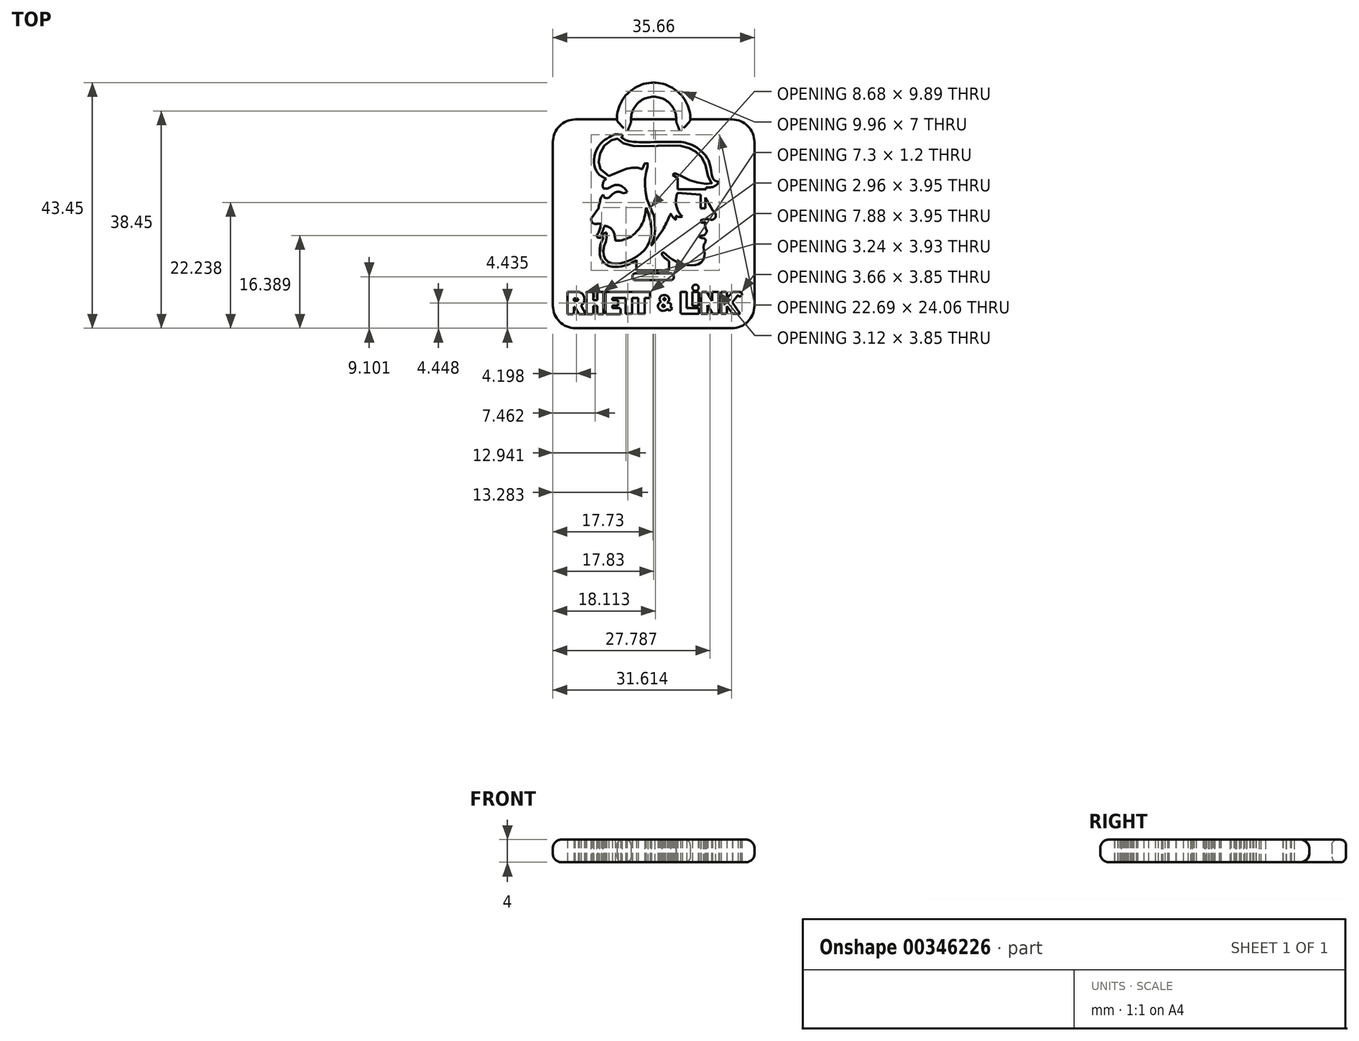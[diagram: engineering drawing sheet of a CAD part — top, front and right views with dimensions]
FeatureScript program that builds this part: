
annotation { "Feature Type Name" : "Feature", "Feature Type Description" : "" }
export const myFeature = defineFeature(function(context is Context, id is Id, definition is map)
    precondition{}
    {
        {
            var Q0;
            Q0=qCreatedBy(makeId("Top.planeOp"),FACE);
            var sketch = newSketch(context, id + "F0", { "sketchPlane" : qUnion([Q0])});
            skFitSpline(sketch, "E0", {"points": [v(13.7, 33.26) * mm, v(12.24, 34.54) * mm, v(11.94, 35.46) * mm, v(12.01, 36.74) * mm, v(12.51, 38.04) * mm, v(13.53, 39.18) * mm, v(14.57, 39.78) * mm, v(15.22, 39.92) * mm, v(15.44, 39.53) * mm, v(17.1, 38.8) * mm, v(18.7, 38.6) * mm, v(21.72, 38.6) * mm, v(24.02, 38.67) * mm, v(26.42, 38.61) * mm, v(27.65, 38.32) * mm, v(28.66, 37.89) * mm, v(29.6, 37.23) * mm, v(30.3, 36.36) * mm, v(30.89, 35.02) * mm, v(31.44, 32.77) * mm, v(31.88, 31.99) * mm, v(31.48, 31.9) * mm, v(30.69, 31.9) * mm, v(29.3, 32.16) * mm, v(28.17, 32.45) * mm, v(27.15, 32.9) * mm, v(25.4, 33.87) * mm, v(25.3, 33.81) * mm], "startDerivative": vector(-77.71, 44.4) * mm, "endDerivative": vector(-18.68, -15.52) * mm});
            skLineSegment(sketch, "E1", {"start": v(25.3, 33.81) * mm, "end": v(25.02, 33.46) * mm});
            skLineSegment(sketch, "E2", {"start": v(25.02, 33.46) * mm, "end": v(25.9, 32.88) * mm});
            skLineSegment(sketch, "E3", {"start": v(25.9, 32.88) * mm, "end": v(25.9, 30.92) * mm});
            skLineSegment(sketch, "E4", {"start": v(25.9, 30.92) * mm, "end": v(30.9, 30.92) * mm});
            skLineSegment(sketch, "E5", {"start": v(30.9, 30.92) * mm, "end": v(30.9, 31.22) * mm});
            skLineSegment(sketch, "E6", {"start": v(30.9, 31.22) * mm, "end": v(31.24, 31.22) * mm});
            skLineSegment(sketch, "E7", {"start": v(25.87, 30.3) * mm, "end": v(29.94, 29.97) * mm});
            skLineSegment(sketch, "E8", {"start": v(29.94, 29.97) * mm, "end": v(29.94, 27.54) * mm});
            skLineSegment(sketch, "E9", {"start": v(29.94, 27.54) * mm, "end": v(30.81, 27.54) * mm});
            skLineSegment(sketch, "E10", {"start": v(30.81, 27.54) * mm, "end": v(30.81, 29.46) * mm});
            skLineSegment(sketch, "E11", {"start": v(30.81, 29.46) * mm, "end": v(31.98, 27.34) * mm});
            skLineSegment(sketch, "E12", {"start": v(18.62, 18.44) * mm, "end": v(18.62, 16.55) * mm});
            skLineSegment(sketch, "E13", {"start": v(18.62, 16.55) * mm, "end": v(24.35, 16.55) * mm});
            skLineSegment(sketch, "E14", {"start": v(24.35, 16.55) * mm, "end": v(24.35, 18.23) * mm});
            skLineSegment(sketch, "E15.bottom", {"start": v(18.4, 16.04) * mm, "end": v(24.7, 16.04) * mm});
            skLineSegment(sketch, "E15.top", {"start": v(18.4, 14.84) * mm, "end": v(24.7, 14.84) * mm});
            skLineSegment(sketch, "E15.left", {"start": v(17.9, 15.54) * mm, "end": v(17.9, 15.34) * mm});
            skLineSegment(sketch, "E15.right", {"start": v(25.2, 15.54) * mm, "end": v(25.2, 15.34) * mm});
            skPoint(sketch, "E16.visualSharp", {"position": v(17.9, 16.04) * mm});
            skArc(sketch, "E16.filletArc", {"start": v(18.4, 16.04) * mm, "mid": v(18.05, 15.9) * mm, "end": v(17.9, 15.54) * mm});
            skPoint(sketch, "E17.visualSharp", {"position": v(17.9, 14.84) * mm});
            skArc(sketch, "E17.filletArc", {"start": v(17.9, 15.34) * mm, "mid": v(18.05, 14.99) * mm, "end": v(18.4, 14.84) * mm});
            skPoint(sketch, "E18.visualSharp", {"position": v(25.2, 16.04) * mm});
            skArc(sketch, "E18.filletArc", {"start": v(25.2, 15.54) * mm, "mid": v(25.05, 15.9) * mm, "end": v(24.7, 16.04) * mm});
            skPoint(sketch, "E19.visualSharp", {"position": v(25.2, 14.84) * mm});
            skArc(sketch, "E19.filletArc", {"start": v(24.7, 14.84) * mm, "mid": v(25.05, 14.99) * mm, "end": v(25.2, 15.34) * mm});
            skLineSegment(sketch, "E20", {"start": v(7.22, 8.81) * mm, "end": v(6.4, 8.81) * mm});
            skLineSegment(sketch, "E21", {"start": v(6.4, 8.81) * mm, "end": v(6.4, 12.74) * mm});
            skLineSegment(sketch, "E22", {"start": v(6.4, 12.74) * mm, "end": v(8.5, 12.74) * mm});
            skLineSegment(sketch, "E23", {"start": v(8.07, 11.6) * mm, "end": v(7.55, 11.6) * mm});
            skLineSegment(sketch, "E24", {"start": v(7.55, 11.6) * mm, "end": v(7.55, 11.18) * mm});
            skLineSegment(sketch, "E25", {"start": v(7.55, 11.18) * mm, "end": v(8.07, 11.18) * mm});
            skLineSegment(sketch, "E26", {"start": v(7.52, 9.11) * mm, "end": v(7.52, 10.11) * mm});
            skLineSegment(sketch, "E27", {"start": v(7.52, 10.11) * mm, "end": v(7.74, 10.11) * mm});
            skLineSegment(sketch, "E28", {"start": v(7.74, 10.11) * mm, "end": v(8.45, 8.81) * mm});
            skLineSegment(sketch, "E29", {"start": v(8.45, 8.81) * mm, "end": v(9.64, 8.81) * mm});
            skLineSegment(sketch, "E30", {"start": v(10.96, 11.31) * mm, "end": v(10.96, 12.46) * mm});
            skLineSegment(sketch, "E31", {"start": v(10.66, 12.76) * mm, "end": v(9.8, 12.76) * mm});
            skLineSegment(sketch, "E32", {"start": v(9.8, 12.76) * mm, "end": v(9.8, 8.81) * mm});
            skLineSegment(sketch, "E33", {"start": v(9.8, 8.81) * mm, "end": v(10.66, 8.81) * mm});
            skLineSegment(sketch, "E34", {"start": v(10.96, 9.11) * mm, "end": v(10.96, 10.29) * mm});
            skLineSegment(sketch, "E35", {"start": v(10.96, 10.29) * mm, "end": v(11.7, 10.29) * mm});
            skLineSegment(sketch, "E36", {"start": v(11.7, 10.29) * mm, "end": v(11.7, 9.11) * mm});
            skLineSegment(sketch, "E37", {"start": v(12, 8.81) * mm, "end": v(12.76, 8.81) * mm});
            skLineSegment(sketch, "E38", {"start": v(12.76, 8.81) * mm, "end": v(12.76, 12.76) * mm});
            skLineSegment(sketch, "E39", {"start": v(12.76, 12.76) * mm, "end": v(12, 12.76) * mm});
            skLineSegment(sketch, "E40", {"start": v(11.7, 12.46) * mm, "end": v(11.7, 11.31) * mm});
            skLineSegment(sketch, "E41", {"start": v(11.7, 11.31) * mm, "end": v(10.96, 11.31) * mm});
            skLineSegment(sketch, "E42", {"start": v(13.16, 12.46) * mm, "end": v(13.16, 9.11) * mm});
            skLineSegment(sketch, "E43", {"start": v(13.46, 8.81) * mm, "end": v(15.8, 8.81) * mm});
            skLineSegment(sketch, "E44", {"start": v(15.8, 8.81) * mm, "end": v(15.8, 9.6) * mm});
            skLineSegment(sketch, "E45", {"start": v(15.5, 9.9) * mm, "end": v(14.31, 9.9) * mm});
            skLineSegment(sketch, "E46", {"start": v(14.31, 9.9) * mm, "end": v(14.31, 10.36) * mm});
            skLineSegment(sketch, "E47", {"start": v(14.31, 10.36) * mm, "end": v(15.38, 10.36) * mm});
            skLineSegment(sketch, "E48", {"start": v(15.38, 10.36) * mm, "end": v(15.38, 11.28) * mm});
            skLineSegment(sketch, "E49", {"start": v(15.38, 11.28) * mm, "end": v(14.31, 11.28) * mm});
            skLineSegment(sketch, "E50", {"start": v(14.31, 11.28) * mm, "end": v(14.31, 11.71) * mm});
            skLineSegment(sketch, "E51", {"start": v(14.31, 11.71) * mm, "end": v(16.7, 11.71) * mm});
            skLineSegment(sketch, "E52", {"start": v(16.7, 11.71) * mm, "end": v(16.7, 8.91) * mm});
            skLineSegment(sketch, "E53", {"start": v(16.7, 8.91) * mm, "end": v(17.85, 8.91) * mm});
            skLineSegment(sketch, "E54", {"start": v(17.85, 8.91) * mm, "end": v(17.85, 11.71) * mm});
            skLineSegment(sketch, "E55", {"start": v(17.85, 11.71) * mm, "end": v(18.92, 11.71) * mm});
            skLineSegment(sketch, "E56", {"start": v(18.92, 11.71) * mm, "end": v(18.92, 8.91) * mm});
            skLineSegment(sketch, "E57", {"start": v(18.92, 8.91) * mm, "end": v(20.05, 8.91) * mm});
            skLineSegment(sketch, "E58", {"start": v(20.05, 8.91) * mm, "end": v(20.05, 11.71) * mm});
            skLineSegment(sketch, "E59", {"start": v(20.05, 11.71) * mm, "end": v(21.04, 11.71) * mm});
            skLineSegment(sketch, "E60", {"start": v(21.04, 11.71) * mm, "end": v(21.04, 12.76) * mm});
            skLineSegment(sketch, "E61", {"start": v(21.04, 12.76) * mm, "end": v(13.46, 12.76) * mm});
            skLineSegment(sketch, "E62", {"start": v(24.07, 9.75) * mm, "end": v(24.43, 9.42) * mm});
            skLineSegment(sketch, "E63", {"start": v(24.43, 9.42) * mm, "end": v(24.95, 9.86) * mm});
            skLineSegment(sketch, "E64", {"start": v(24.95, 9.86) * mm, "end": v(24.58, 10.2) * mm});
            skLineSegment(sketch, "E65", {"start": v(24.58, 10.2) * mm, "end": v(24.85, 10.5) * mm});
            skLineSegment(sketch, "E66", {"start": v(24.85, 10.5) * mm, "end": v(24.44, 10.87) * mm});
            skLineSegment(sketch, "E67", {"start": v(24.44, 10.87) * mm, "end": v(24.22, 10.72) * mm});
            skLineSegment(sketch, "E68", {"start": v(24.22, 10.72) * mm, "end": v(24.06, 10.86) * mm});
            skLineSegment(sketch, "E69", {"start": v(23.67, 10.23) * mm, "end": v(23.35, 10.55) * mm});
            skLineSegment(sketch, "E70", {"start": v(26.4, 12.76) * mm, "end": v(26.4, 9.21) * mm});
            skLineSegment(sketch, "E71", {"start": v(26.7, 8.91) * mm, "end": v(29.66, 8.91) * mm});
            skLineSegment(sketch, "E72", {"start": v(29.66, 8.91) * mm, "end": v(29.66, 9.9) * mm});
            skLineSegment(sketch, "E73", {"start": v(29.66, 9.9) * mm, "end": v(27.5, 9.9) * mm});
            skLineSegment(sketch, "E74", {"start": v(27.5, 9.9) * mm, "end": v(27.5, 12.76) * mm});
            skLineSegment(sketch, "E75", {"start": v(27.5, 12.76) * mm, "end": v(26.4, 12.76) * mm});
            skLineSegment(sketch, "E76", {"start": v(28.51, 12.76) * mm, "end": v(28.51, 10.27) * mm});
            skLineSegment(sketch, "E77", {"start": v(28.51, 10.27) * mm, "end": v(29.61, 10.27) * mm});
            skLineSegment(sketch, "E78", {"start": v(29.61, 10.27) * mm, "end": v(29.61, 12.76) * mm});
            skLineSegment(sketch, "E79", {"start": v(29.61, 12.76) * mm, "end": v(28.51, 12.76) * mm});
            skCircle(sketch, "E80", {"center": v(29.06, 13.5) * mm, "radius": 0.55 * mm});
            skLineSegment(sketch, "E81", {"start": v(30.05, 8.91) * mm, "end": v(30.05, 12.46) * mm});
            skLineSegment(sketch, "E82", {"start": v(30.35, 12.76) * mm, "end": v(31.01, 12.76) * mm});
            skLineSegment(sketch, "E83", {"start": v(31.01, 12.76) * mm, "end": v(32, 11.17) * mm});
            skLineSegment(sketch, "E84", {"start": v(32, 11.17) * mm, "end": v(32, 12.76) * mm});
            skLineSegment(sketch, "E85", {"start": v(32, 12.76) * mm, "end": v(33.17, 12.76) * mm});
            skLineSegment(sketch, "E86", {"start": v(33.17, 12.76) * mm, "end": v(33.17, 9.21) * mm});
            skLineSegment(sketch, "E87", {"start": v(32.87, 8.91) * mm, "end": v(32.08, 8.91) * mm});
            skLineSegment(sketch, "E88", {"start": v(32.08, 8.91) * mm, "end": v(31.15, 10.42) * mm});
            skLineSegment(sketch, "E89", {"start": v(31.15, 10.42) * mm, "end": v(31.15, 8.91) * mm});
            skLineSegment(sketch, "E90", {"start": v(31.15, 8.91) * mm, "end": v(30.05, 8.91) * mm});
            skLineSegment(sketch, "E91", {"start": v(33.6, 12.76) * mm, "end": v(33.6, 8.91) * mm});
            skLineSegment(sketch, "E92", {"start": v(33.6, 8.91) * mm, "end": v(34.32, 8.91) * mm});
            skLineSegment(sketch, "E93", {"start": v(34.62, 9.21) * mm, "end": v(34.62, 10.23) * mm});
            skLineSegment(sketch, "E94", {"start": v(34.62, 10.23) * mm, "end": v(35.62, 8.91) * mm});
            skLineSegment(sketch, "E95", {"start": v(35.62, 8.91) * mm, "end": v(36.94, 8.91) * mm});
            skLineSegment(sketch, "E96", {"start": v(36.94, 8.91) * mm, "end": v(35.54, 10.93) * mm});
            skLineSegment(sketch, "E97", {"start": v(35.54, 10.93) * mm, "end": v(37, 12.76) * mm});
            skLineSegment(sketch, "E98", {"start": v(37, 12.76) * mm, "end": v(35.6, 12.76) * mm});
            skLineSegment(sketch, "E99", {"start": v(35.6, 12.76) * mm, "end": v(34.62, 11.63) * mm});
            skLineSegment(sketch, "E100", {"start": v(34.62, 11.63) * mm, "end": v(34.62, 12.46) * mm});
            skLineSegment(sketch, "E101", {"start": v(34.32, 12.76) * mm, "end": v(33.6, 12.76) * mm});
            skCircle(sketch, "E102", {"center": v(36.9, 12.33) * mm, "radius": 0.37 * mm});
            skArc(sketch, "E103", {"start": v(8.07, 11.6) * mm, "mid": v(8.29, 11.39) * mm, "end": v(8.07, 11.18) * mm});
            skPoint(sketch, "E104.visualSharp", {"position": v(7.52, 8.81) * mm});
            skArc(sketch, "E104.filletArc", {"start": v(7.22, 8.81) * mm, "mid": v(7.44, 8.9) * mm, "end": v(7.52, 9.11) * mm});
            skPoint(sketch, "E105.visualSharp", {"position": v(10.96, 8.81) * mm});
            skArc(sketch, "E105.filletArc", {"start": v(10.66, 8.81) * mm, "mid": v(10.88, 8.9) * mm, "end": v(10.96, 9.11) * mm});
            skPoint(sketch, "E106.visualSharp", {"position": v(11.7, 8.81) * mm});
            skArc(sketch, "E106.filletArc", {"start": v(11.7, 9.11) * mm, "mid": v(11.79, 8.9) * mm, "end": v(12, 8.81) * mm});
            skPoint(sketch, "E107.visualSharp", {"position": v(10.96, 12.76) * mm});
            skArc(sketch, "E107.filletArc", {"start": v(10.96, 12.46) * mm, "mid": v(10.88, 12.68) * mm, "end": v(10.66, 12.76) * mm});
            skPoint(sketch, "E108.visualSharp", {"position": v(11.7, 12.76) * mm});
            skArc(sketch, "E108.filletArc", {"start": v(12, 12.76) * mm, "mid": v(11.79, 12.68) * mm, "end": v(11.7, 12.46) * mm});
            skPoint(sketch, "E109.visualSharp", {"position": v(13.16, 8.81) * mm});
            skArc(sketch, "E109.filletArc", {"start": v(13.16, 9.11) * mm, "mid": v(13.25, 8.9) * mm, "end": v(13.46, 8.81) * mm});
            skPoint(sketch, "E110.visualSharp", {"position": v(13.16, 12.76) * mm});
            skArc(sketch, "E110.filletArc", {"start": v(13.46, 12.76) * mm, "mid": v(13.25, 12.68) * mm, "end": v(13.16, 12.46) * mm});
            skPoint(sketch, "E111.visualSharp", {"position": v(15.8, 9.9) * mm});
            skArc(sketch, "E111.filletArc", {"start": v(15.8, 9.6) * mm, "mid": v(15.71, 9.81) * mm, "end": v(15.5, 9.9) * mm});
            skPoint(sketch, "E112.visualSharp", {"position": v(26.4, 8.91) * mm});
            skArc(sketch, "E112.filletArc", {"start": v(26.4, 9.21) * mm, "mid": v(26.48, 9) * mm, "end": v(26.7, 8.91) * mm});
            skPoint(sketch, "E113.visualSharp", {"position": v(33.17, 8.91) * mm});
            skArc(sketch, "E113.filletArc", {"start": v(32.87, 8.91) * mm, "mid": v(33.08, 9) * mm, "end": v(33.17, 9.21) * mm});
            skPoint(sketch, "E114.visualSharp", {"position": v(30.05, 12.76) * mm});
            skArc(sketch, "E114.filletArc", {"start": v(30.35, 12.76) * mm, "mid": v(30.13, 12.68) * mm, "end": v(30.05, 12.46) * mm});
            skPoint(sketch, "E115.visualSharp", {"position": v(34.62, 8.91) * mm});
            skArc(sketch, "E115.filletArc", {"start": v(34.32, 8.91) * mm, "mid": v(34.53, 9) * mm, "end": v(34.62, 9.21) * mm});
            skPoint(sketch, "E116.visualSharp", {"position": v(34.62, 12.76) * mm});
            skArc(sketch, "E116.filletArc", {"start": v(34.62, 12.46) * mm, "mid": v(34.53, 12.68) * mm, "end": v(34.32, 12.76) * mm});
            skLineSegment(sketch, "E117", {"start": v(9.64, 8.81) * mm, "end": v(8.8, 10.36) * mm});
            skFitSpline(sketch, "E118", {"points": [v(8.5, 12.74) * mm, v(9.01, 12.48) * mm, v(9.36, 11.79) * mm, v(9.33, 11) * mm, v(9.14, 10.66) * mm, v(8.8, 10.36) * mm], "startDerivative": vector(2.6, -0.63) * mm, "endDerivative": vector(-2.15, -1.69) * mm});
            skFitSpline(sketch, "E119", {"points": [v(24.07, 9.75) * mm, v(23.83, 9.54) * mm, v(23.13, 9.45) * mm, v(22.51, 9.85) * mm, v(22.4, 10.32) * mm, v(22.56, 10.69) * mm, v(22.9, 11.02) * mm, v(22.7, 11.3) * mm, v(22.73, 11.77) * mm, v(22.97, 12.07) * mm, v(23.5, 12.23) * mm, v(24.18, 12) * mm, v(24.4, 11.48) * mm, v(24.32, 11.18) * mm, v(24.06, 10.86) * mm], "startDerivative": vector(-3.34, -4.2) * mm, "endDerivative": vector(-4.48, -5) * mm});
            skFitSpline(sketch, "E120", {"points": [v(23.67, 10.23) * mm, v(23.47, 10.11) * mm, v(23.28, 10.12) * mm, v(23.18, 10.25) * mm, v(23.22, 10.44) * mm, v(23.35, 10.55) * mm], "startDerivative": vector(-0.9, -0.65) * mm, "endDerivative": vector(0.88, 0.4) * mm});
            skCircle(sketch, "E121", {"center": v(23.57, 11.47) * mm, "radius": 0.18 * mm});
            skLineSegment(sketch, "E122", {"start": v(0, 0) * mm, "end": v(0, 43.3) * mm});
            skLineSegment(sketch, "E123", {"start": v(0, 43.3) * mm, "end": v(43.3, 43.3) * mm});
            skLineSegment(sketch, "E124", {"start": v(43.3, 0) * mm, "end": v(0, 0) * mm});
            skLineSegment(sketch, "E125", {"start": v(43.3, 43.3) * mm, "end": v(43.3, 0) * mm});
            skFitSpline(sketch, "E126", {"points": [v(13.7, 33.26) * mm, v(14.23, 33.5) * mm, v(16.47, 34.43) * mm, v(18.04, 34.76) * mm, v(19.3, 34.63) * mm, v(19.71, 34.46) * mm, v(19.84, 34.98) * mm, v(20.13, 35.54) * mm, v(20.53, 35.54) * mm, v(20.66, 35.28) * mm, v(20.4, 34.4) * mm, v(20.12, 32.33) * mm, v(20.21, 30.35) * mm, v(20.66, 28.65) * mm, v(21.4, 26.93) * mm, v(21.78, 25.9) * mm, v(21.86, 23.35) * mm, v(21.62, 22.03) * mm, v(21.27, 21.02) * mm, v(21.27, 21) * mm], "startDerivative": vector(10.47, 5.06) * mm, "endDerivative": vector(0.53, -1.97) * mm});
            skFitSpline(sketch, "E127", {"points": [v(21.27, 21) * mm, v(22.62, 22.8) * mm, v(23.76, 24.7) * mm, v(24.68, 26.6) * mm, v(24.68, 26.58) * mm], "startDerivative": vector(4.32, 5.63) * mm, "endDerivative": vector(-0.14, -0.95) * mm});
            skFitSpline(sketch, "E128", {"points": [v(24.68, 26.58) * mm, v(25.07, 25.98) * mm, v(25.56, 25.5) * mm], "startDerivative": vector(0.72, -1.24) * mm, "endDerivative": vector(1.04, -0.9) * mm});
            skFitSpline(sketch, "E129", {"points": [v(25.56, 25.5) * mm, v(25.56, 26.26) * mm], "startDerivative": vector(0, 0.75) * mm, "endDerivative": vector(0, 0.75) * mm});
            skFitSpline(sketch, "E130", {"points": [v(25.56, 26.26) * mm, v(25.86, 26.1) * mm, v(26.16, 26.04) * mm, v(26.74, 26.09) * mm], "startDerivative": vector(1, -0.51) * mm, "endDerivative": vector(1.53, 0.33) * mm});
            skFitSpline(sketch, "E131", {"points": [v(26.74, 26.09) * mm, v(26.38, 26.45) * mm, v(25.95, 27.13) * mm, v(25.67, 27.93) * mm, v(25.6, 28.8) * mm, v(25.67, 29.55) * mm, v(25.77, 30.03) * mm, v(25.87, 30.3) * mm], "startDerivative": vector(-2.78, 2.36) * mm, "endDerivative": vector(1, 2.58) * mm});
            skFitSpline(sketch, "E132", {"points": [v(13, 24.5) * mm, v(13.66, 24.25) * mm, v(14.33, 23.75) * mm, v(14.76, 22.72) * mm, v(14.88, 21.85) * mm], "startDerivative": vector(2.88, -0.99) * mm, "endDerivative": vector(0.35, -3.2) * mm});
            skFitSpline(sketch, "E133", {"points": [v(14.88, 21.85) * mm, v(15.7, 21.85) * mm, v(16.83, 22.17) * mm, v(18.11, 22.92) * mm, v(19.39, 24.4) * mm, v(19.96, 25.77) * mm, v(20.31, 27.67) * mm], "startDerivative": vector(5.77, -0.25) * mm, "endDerivative": vector(1.55, 10.31) * mm});
            skFitSpline(sketch, "E134", {"points": [v(20.31, 27.67) * mm, v(20.79, 26.42) * mm, v(21.14, 25.1) * mm, v(21.16, 22.75) * mm, v(20.51, 20.87) * mm, v(19.66, 19.85) * mm, v(18.45, 18.9) * mm, v(16.81, 18.12) * mm, v(15.41, 17.8) * mm, v(14.26, 17.85) * mm, v(13.45, 18.2) * mm, v(12.93, 18.85) * mm, v(12.73, 19.75) * mm, v(12.96, 21.07) * mm, v(13.28, 22.1) * mm, v(13.3, 23.27) * mm], "startDerivative": vector(7.48, -19.02) * mm, "endDerivative": vector(-1, 19.55) * mm});
            skFitSpline(sketch, "E135", {"points": [v(13.3, 23.27) * mm, v(12.42, 22.94) * mm], "startDerivative": vector(-0.75, -0.25) * mm, "endDerivative": vector(-0.75, -0.25) * mm});
            skFitSpline(sketch, "E136", {"points": [v(12.42, 22.94) * mm, v(12.68, 23.66) * mm, v(13, 24.5) * mm], "startDerivative": vector(-0.16, 1.21) * mm, "endDerivative": vector(1, 1.71) * mm});
            skFitSpline(sketch, "E137", {"points": [v(18.62, 18.44) * mm, v(17.83, 17.95) * mm, v(16.87, 17.5) * mm, v(15.67, 17.23) * mm, v(14.53, 17.19) * mm, v(13.84, 17.32) * mm, v(13.02, 17.77) * mm, v(12.35, 18.68) * mm, v(12.1, 19.88) * mm, v(12.22, 20.98) * mm, v(12.5, 21.78) * mm, v(12.73, 22.45) * mm, v(12.73, 22.47) * mm], "startDerivative": vector(-8.75, -6.28) * mm, "endDerivative": vector(-0.27, 0.92) * mm});
            skFitSpline(sketch, "E138", {"points": [v(12.74, 22.46) * mm, v(12.38, 22.4) * mm, v(12.05, 22.33) * mm, v(11.71, 22.46) * mm, v(11.61, 22.67) * mm, v(11.75, 22.98) * mm, v(12.04, 23.63) * mm, v(12.35, 24.77) * mm], "startDerivative": vector(-2.79, -0.06) * mm, "endDerivative": vector(1.35, 5.3) * mm});
            skFitSpline(sketch, "E139", {"points": [v(12.35, 24.77) * mm, v(11.92, 24.86) * mm, v(11.52, 24.8) * mm, v(10.95, 24.89) * mm, v(10.68, 25.23) * mm, v(10.58, 25.62) * mm, v(10.7, 25.93) * mm], "startDerivative": vector(-1.92, 1.13) * mm, "endDerivative": vector(1.22, 2.03) * mm});
            skFitSpline(sketch, "E140", {"points": [v(10.7, 25.93) * mm, v(10.98, 26.29) * mm, v(11.65, 27.2) * mm, v(11.81, 27.37) * mm, v(11.98, 28.09) * mm, v(12.19, 28.92) * mm, v(12.37, 29.53) * mm, v(12.75, 29.97) * mm], "startDerivative": vector(1.96, 2.27) * mm, "endDerivative": vector(2.76, 3.12) * mm});
            skFitSpline(sketch, "E141", {"points": [v(12.75, 29.97) * mm, v(12.75, 29.75) * mm, v(13.05, 29.4) * mm, v(13.48, 29.38) * mm, v(13.91, 29.6) * mm, v(14.5, 30.14) * mm, v(14.97, 30.44) * mm, v(15.43, 30.5) * mm, v(15.8, 30.4) * mm, v(16.1, 30.3) * mm, v(16.5, 30.26) * mm, v(16.98, 30.44) * mm], "startDerivative": vector(-0.76, -3.33) * mm, "endDerivative": vector(4.38, 2.95) * mm});
            skFitSpline(sketch, "E142", {"points": [v(16.98, 30.44) * mm, v(16.68, 30.91) * mm, v(16.17, 31.36) * mm, v(15.68, 31.6) * mm, v(15.16, 31.71) * mm, v(14.42, 31.52) * mm, v(13.76, 31.2) * mm, v(13.51, 31.07) * mm, v(12.77, 31.07) * mm], "startDerivative": vector(-2.12, 3.97) * mm, "endDerivative": vector(-6.18, 0.38) * mm});
            skFitSpline(sketch, "E143", {"points": [v(12.77, 31.07) * mm, v(12.65, 31.46) * mm, v(12.7, 32.06) * mm, v(12.92, 32.52) * mm, v(13.27, 32.76) * mm], "startDerivative": vector(-0.68, 1.65) * mm, "endDerivative": vector(1.6, 0.77) * mm});
            skFitSpline(sketch, "E144", {"points": [v(13.27, 32.76) * mm, v(12.35, 33.25) * mm, v(11.67, 33.97) * mm, v(11.2, 34.93) * mm, v(11.1, 36.05) * mm, v(11.46, 37.69) * mm, v(12.46, 39.2) * mm, v(13.28, 39.84) * mm, v(14.02, 40.29) * mm, v(14.7, 40.57) * mm, v(15.94, 40.6) * mm], "startDerivative": vector(-9.18, 3.67) * mm, "endDerivative": vector(13, -3.1) * mm});
            skFitSpline(sketch, "E145", {"points": [v(15.94, 40.6) * mm, v(16.1, 40.48) * mm, v(16.12, 40.32) * mm, v(15.94, 40.15) * mm], "startDerivative": vector(0.46, -0.36) * mm, "endDerivative": vector(-0.49, -0.44) * mm});
            skFitSpline(sketch, "E146", {"points": [v(15.94, 40.15) * mm, v(16.15, 39.95) * mm, v(16.67, 39.66) * mm, v(17.65, 39.38) * mm, v(19.08, 39.27) * mm, v(21.9, 39.29) * mm, v(24.27, 39.32) * mm, v(25.9, 39.3) * mm, v(26.9, 39.23) * mm], "startDerivative": vector(2.46, -3.44) * mm, "endDerivative": vector(7.37, -1.77) * mm});
            skFitSpline(sketch, "E147", {"points": [v(26.9, 39.23) * mm, v(27.29, 39.14) * mm, v(27.89, 38.96) * mm, v(28.58, 38.7) * mm, v(29.56, 38.12) * mm, v(30.34, 37.45) * mm, v(30.9, 36.77) * mm, v(31.35, 36.06) * mm, v(31.62, 35.26) * mm, v(31.78, 34.4) * mm, v(31.86, 33.8) * mm, v(32.05, 33.13) * mm, v(32.3, 32.62) * mm, v(32.66, 32.35) * mm, v(33.28, 32.26) * mm], "startDerivative": vector(8.14, -1.9) * mm, "endDerivative": vector(12.08, 0.22) * mm});
            skFitSpline(sketch, "E148", {"points": [v(31.24, 31.22) * mm, v(31.77, 31.27) * mm, v(32.43, 31.47) * mm, v(32.83, 31.75) * mm, v(33.28, 32.26) * mm], "startDerivative": vector(2.05, 0.42) * mm, "endDerivative": vector(1.61, 2.07) * mm});
            skFitSpline(sketch, "E149", {"points": [v(31.98, 27.34) * mm, v(32.1, 27.16) * mm, v(32.2, 27.09) * mm, v(32.48, 26.79) * mm, v(32.62, 26.43) * mm, v(32.59, 26.02) * mm, v(32.39, 25.72) * mm, v(32.14, 25.55) * mm, v(31.9, 25.51) * mm, v(31.55, 25.6) * mm, v(31.08, 25.64) * mm, v(30.67, 25.6) * mm, v(30.26, 25.54) * mm, v(30.04, 25.44) * mm, v(30.02, 25.2) * mm, v(30.08, 25.03) * mm, v(30.36, 25.01) * mm, v(30.7, 25.14) * mm], "startDerivative": vector(1.8, -4.02) * mm, "endDerivative": vector(5.15, 2.14) * mm});
            skFitSpline(sketch, "E150", {"points": [v(30.7, 25.14) * mm, v(30.82, 25.05) * mm, v(30.76, 24.81) * mm, v(30.76, 24.52) * mm, v(30.82, 24.17) * mm, v(30.93, 23.82) * mm, v(31.02, 23.62) * mm, v(30.98, 23.3) * mm, v(30.8, 23.02) * mm, v(30.53, 22.82) * mm, v(30.15, 22.73) * mm, v(29.84, 22.68) * mm, v(29.52, 22.68) * mm], "startDerivative": vector(2.74, -1) * mm, "endDerivative": vector(-3.82, 0.13) * mm});
            skFitSpline(sketch, "E151", {"points": [v(29.52, 22.68) * mm, v(29.69, 22.5) * mm, v(29.94, 22.35) * mm, v(30.16, 22.3) * mm, v(30.5, 22.27) * mm, v(30.76, 22.18) * mm, v(30.88, 21.95) * mm, v(30.87, 21.6) * mm, v(30.62, 21.3) * mm, v(30.5, 21.1) * mm, v(30.45, 20.71) * mm, v(30.54, 20.15) * mm, v(30.63, 19.61) * mm, v(30.62, 18.97) * mm, v(30.44, 18.48) * mm, v(30.12, 18.08) * mm, v(29.67, 17.7) * mm, v(29.28, 17.55) * mm, v(28.7, 17.46) * mm, v(27.65, 17.49) * mm, v(27.02, 17.63) * mm, v(26.42, 17.84) * mm, v(25.7, 18.13) * mm, v(24.84, 18.6) * mm, v(24.21, 19.04) * mm, v(23.56, 19.59) * mm, v(23.49, 19.66) * mm], "startDerivative": vector(5.37, -7) * mm, "endDerivative": vector(-2.84, 3.09) * mm});
            skFitSpline(sketch, "E152", {"points": [v(24.35, 18.23) * mm, v(23.87, 18.59) * mm, v(23.48, 18.9) * mm, v(23.15, 19.3) * mm, v(23.1, 19.6) * mm, v(23.3, 19.73) * mm, v(23.49, 19.66) * mm], "startDerivative": vector(-2.14, 1.54) * mm, "endDerivative": vector(1.45, -0.91) * mm});
            skArc(sketch, "E153", {"start": v(28.15, 43.3) * mm, "mid": v(21.65, 49.8) * mm, "end": v(15.15, 43.3) * mm});
            skArc(sketch, "E154", {"start": v(25.65, 43.3) * mm, "mid": v(21.65, 47.3) * mm, "end": v(17.65, 43.3) * mm});
            skLineSegment(sketch, "E155", {"start": v(3.82, 43.3) * mm, "end": v(3.82, 6.34) * mm});
            skLineSegment(sketch, "E156", {"start": v(3.82, 6.34) * mm, "end": v(39.48, 6.34) * mm});
            skLineSegment(sketch, "E157", {"start": v(39.48, 6.34) * mm, "end": v(39.48, 43.3) * mm});
            skLineSegment(sketch, "E158", {"start": v(3.82, 43.3) * mm, "end": v(39.48, 43.3) * mm, "construction": true});
            skLineSegment(sketch, "E159", {"start": v(10.9, 43.3) * mm, "end": v(3.82, 43.3) * mm});
            skSolve(sketch);
        }
        {
            var Q0;
            Q0=makeQuery(id+"F0.imprint","IMPRINT",FACE,{"disambiguationData":[TD([[makeQuery(id+"F0.imprint","IMPRINT",EDGE,{"derivedFrom":sQuery(id+"F0.wireOp",EDGE,"E0")}),-1.0]])]});
            var Q1;
            Q1=makeQuery(id+"F0.imprint","IMPRINT",FACE,{"disambiguationData":[TD([[makeQuery(id+"F0.imprint","IMPRINT",EDGE,{"derivedFrom":sQuery(id+"F0.wireOp",EDGE,"E132")}),-1.0]])]});
            var Q2;
            Q2=makeQuery(id+"F0.imprint","IMPRINT",FACE,{"disambiguationData":[TD([[makeQuery(id+"F0.imprint","IMPRINT",EDGE,{"derivedFrom":sQuery(id+"F0.wireOp",EDGE,"E23")}),1.0]])]});
            var Q3;
            Q3=makeQuery(id+"F0.imprint","IMPRINT",FACE,{"disambiguationData":[TD([[makeQuery(id+"F0.imprint","IMPRINT",EDGE,{"derivedFrom":sQuery(id+"F0.wireOp",EDGE,"E69")}),1.0]])]});
            var Q4;
            Q4=makeQuery(id+"F0.imprint","IMPRINT",FACE,{"disambiguationData":[TD([[makeQuery(id+"F0.imprint","IMPRINT",EDGE,{"derivedFrom":sQuery(id+"F0.wireOp",EDGE,"E121")}),1.0]])]});
            var Q5;
            {var subQ0=sQuery(id+"F0.wireOp",EDGE,"E153");Q5=makeQuery(id+"F0.imprint","IMPRINT",FACE,{"disambiguationData":[TD([[makeQuery(id+"F0.imprint","IMPRINT",EDGE,{"derivedFrom":subQ0}),1.0]])]});}
            extrude(context, id + "F1", {"entities" : qUnion([Q0, Q1, Q2, Q3, Q4, Q5]), "depth" : 4 * mm});
        }
        {
            var Q0;
            Q0=makeQuery(id+"F0.imprint","IMPRINT",FACE,{"disambiguationData":[TD([[makeQuery(id+"F0.imprint","IMPRINT",EDGE,{"derivedFrom":sQuery(id+"F0.wireOp",EDGE,"E0")}),1.0]])]});
            var Q1;
            Q1=makeQuery(id+"F0.imprint","IMPRINT",FACE,{"disambiguationData":[TD([[makeQuery(id+"F0.imprint","IMPRINT",EDGE,{"derivedFrom":sQuery(id+"F0.wireOp",EDGE,"E15.bottom")}),-1.0]])]});
            var Q2;
            Q2=makeQuery(id+"F0.imprint","IMPRINT",FACE,{"disambiguationData":[TD([[makeQuery(id+"F0.imprint","IMPRINT",EDGE,{"derivedFrom":sQuery(id+"F0.wireOp",EDGE,"E20")}),-1.0]])]});
            var Q3;
            Q3=makeQuery(id+"F0.imprint","IMPRINT",FACE,{"disambiguationData":[TD([[makeQuery(id+"F0.imprint","IMPRINT",EDGE,{"derivedFrom":sQuery(id+"F0.wireOp",EDGE,"E30")}),1.0]])]});
            var Q4;
            Q4=makeQuery(id+"F0.imprint","IMPRINT",FACE,{"disambiguationData":[TD([[makeQuery(id+"F0.imprint","IMPRINT",EDGE,{"derivedFrom":sQuery(id+"F0.wireOp",EDGE,"E42")}),1.0]])]});
            var Q5;
            Q5=makeQuery(id+"F0.imprint","IMPRINT",FACE,{"disambiguationData":[TD([[makeQuery(id+"F0.imprint","IMPRINT",EDGE,{"derivedFrom":sQuery(id+"F0.wireOp",EDGE,"E62")}),1.0]])]});
            var Q6;
            Q6=makeQuery(id+"F0.imprint","IMPRINT",FACE,{"disambiguationData":[TD([[makeQuery(id+"F0.imprint","IMPRINT",EDGE,{"derivedFrom":sQuery(id+"F0.wireOp",EDGE,"E70")}),1.0]])]});
            var Q7;
            Q7=makeQuery(id+"F0.imprint","IMPRINT",FACE,{"disambiguationData":[TD([[makeQuery(id+"F0.imprint","IMPRINT",EDGE,{"derivedFrom":sQuery(id+"F0.wireOp",EDGE,"E76")}),1.0]])]});
            var Q8;
            Q8=makeQuery(id+"F0.imprint","IMPRINT",FACE,{"disambiguationData":[TD([[makeQuery(id+"F0.imprint","IMPRINT",EDGE,{"derivedFrom":sQuery(id+"F0.wireOp",EDGE,"E80")}),1.0]])]});
            var Q9;
            Q9=makeQuery(id+"F0.imprint","IMPRINT",FACE,{"disambiguationData":[TD([[makeQuery(id+"F0.imprint","IMPRINT",EDGE,{"derivedFrom":sQuery(id+"F0.wireOp",EDGE,"E81")}),-1.0]])]});
            var Q10;
            Q10=makeQuery(id+"F0.imprint","IMPRINT",FACE,{"disambiguationData":[TD([[makeQuery(id+"F0.imprint","IMPRINT",EDGE,{"derivedFrom":sQuery(id+"F0.wireOp",EDGE,"E91")}),1.0]])]});
            var Q11;
            Q11=makeQuery(id+"F0.imprint","IMPRINT",FACE,{"disambiguationData":[TD([[makeQuery(id+"F0.imprint","IMPRINT",EDGE,{"derivedFrom":sQuery(id+"F0.wireOp",EDGE,"E102")}),1.0]])]});
            extrude(context, id + "F2", {"entities" : qUnion([Q0, Q1, Q2, Q3, Q4, Q5, Q6, Q7, Q8, Q9, Q10, Q11]), "depth" : 4 * mm});
        }
        {
            var Q0;
            Q0=makeQuery(id+"F1.opExtrude","CAP_EDGE",EDGE,{"disambiguationData":[OSD([sQuery(id+"F0.wireOp",EDGE,"E122")])],"isStart":false});
            var Q1;
            {var subQ0=sQuery(id+"F0.wireOp",EDGE,"E123");Q1=makeQuery(id+"F1.opExtrude","CAP_EDGE",EDGE,{"disambiguationData":[OSD([subQ0]),TDD([makeQuery(id+"F0.imprint","IMPRINT",EDGE,{"disambiguationData":[TD([[makeQuery(id+"F0.imprint","INTERSECT",VERTEX,{"derivedFrom":[sQuery(id+"F0.wireOp",EDGE,"E122"),subQ0]}),-1.0]])],"derivedFrom":subQ0})])],"isStart":false});}
            var Q2;
            {var subQ0=sQuery(id+"F0.wireOp",EDGE,"E123");Q2=makeQuery(id+"F1.opExtrude","CAP_EDGE",EDGE,{"disambiguationData":[OSD([subQ0]),TDD([makeQuery(id+"F0.imprint","IMPRINT",EDGE,{"disambiguationData":[TD([[makeQuery(id+"F0.imprint","INTERSECT",VERTEX,{"derivedFrom":[subQ0,sQuery(id+"F0.wireOp",EDGE,"E125")]}),1.0]])],"derivedFrom":subQ0})])],"isStart":false});}
            var Q3;
            Q3=makeQuery(id+"F1.opExtrude","CAP_EDGE",EDGE,{"disambiguationData":[OSD([sQuery(id+"F0.wireOp",EDGE,"E125")])],"isStart":false});
            var Q4;
            Q4=makeQuery(id+"F1.opExtrude","CAP_EDGE",EDGE,{"disambiguationData":[OSD([sQuery(id+"F0.wireOp",EDGE,"E124")])],"isStart":false});
            var Q5;
            {var subQ0=sQuery(id+"F0.wireOp",EDGE,"E154");var subQ1=sQuery(id+"F0.wireOp",EDGE,"E123");Q5=makeQuery(id+"F1.opExtrude","CAP_EDGE",EDGE,{"disambiguationData":[OSD([subQ1]),TDD([makeQuery(id+"F0.imprint","IMPRINT",EDGE,{"disambiguationData":[TD([[makeQuery(id+"F0.imprint","INTERSECT",VERTEX,{"disambiguationData":[OD(0.0)],"derivedFrom":[subQ1,subQ0]}),1.0]])],"derivedFrom":subQ1})])],"isStart":false});}
            var Q6;
            {var subQ0=sQuery(id+"F0.wireOp",EDGE,"E123");Q6=makeQuery(id+"F1.opExtrude","CAP_EDGE",EDGE,{"disambiguationData":[OSD([subQ0]),TDD([makeQuery(id+"F0.imprint","IMPRINT",EDGE,{"disambiguationData":[TD([[makeQuery(id+"F0.imprint","INTERSECT",VERTEX,{"derivedFrom":[subQ0,sQuery(id+"F0.wireOp",EDGE,"E125")]}),1.0]])],"derivedFrom":subQ0})])],"isStart":true});}
            var Q7;
            {var subQ0=sQuery(id+"F0.wireOp",EDGE,"E154");var subQ1=sQuery(id+"F0.wireOp",EDGE,"E123");Q7=makeQuery(id+"F1.opExtrude","CAP_EDGE",EDGE,{"disambiguationData":[OSD([subQ1]),TDD([makeQuery(id+"F0.imprint","IMPRINT",EDGE,{"disambiguationData":[TD([[makeQuery(id+"F0.imprint","INTERSECT",VERTEX,{"disambiguationData":[OD(0.0)],"derivedFrom":[subQ1,subQ0]}),1.0]])],"derivedFrom":subQ1})])],"isStart":true});}
            var Q8;
            {var subQ0=sQuery(id+"F0.wireOp",EDGE,"E123");Q8=makeQuery(id+"F1.opExtrude","CAP_EDGE",EDGE,{"disambiguationData":[OSD([subQ0]),TDD([makeQuery(id+"F0.imprint","IMPRINT",EDGE,{"disambiguationData":[TD([[makeQuery(id+"F0.imprint","INTERSECT",VERTEX,{"derivedFrom":[sQuery(id+"F0.wireOp",EDGE,"E122"),subQ0]}),-1.0]])],"derivedFrom":subQ0})])],"isStart":true});}
            var Q9;
            Q9=makeQuery(id+"F1.opExtrude","CAP_EDGE",EDGE,{"disambiguationData":[OSD([sQuery(id+"F0.wireOp",EDGE,"E122")])],"isStart":true});
            var Q10;
            Q10=makeQuery(id+"F1.opExtrude","CAP_EDGE",EDGE,{"disambiguationData":[OSD([sQuery(id+"F0.wireOp",EDGE,"E124")])],"isStart":true});
            var Q11;
            Q11=makeQuery(id+"F1.opExtrude","CAP_EDGE",EDGE,{"disambiguationData":[OSD([sQuery(id+"F0.wireOp",EDGE,"E125")])],"isStart":true});
            fillet(context, id + "F3", {"entities" : qUnion([Q0, Q1, Q2, Q3, Q4, Q5, Q6, Q7, Q8, Q9, Q10, Q11]), "radius" : 2 * mm, "tangentPropagation" : true, "allowEdgeOverflow" : false});
        }
        {
            var Q0;
            Q0=makeQuery(id+"F1.opExtrude","CAP_EDGE",EDGE,{"disambiguationData":[OSD([sQuery(id+"F0.wireOp",EDGE,"E153")])],"isStart":false});
            var Q1;
            Q1=makeQuery(id+"F1.opExtrude","CAP_EDGE",EDGE,{"disambiguationData":[OSD([sQuery(id+"F0.wireOp",EDGE,"E154")])],"isStart":false});
            var Q2;
            Q2=makeQuery(id+"F1.opExtrude","CAP_EDGE",EDGE,{"disambiguationData":[OSD([sQuery(id+"F0.wireOp",EDGE,"E153")])],"isStart":true});
            var Q3;
            Q3=makeQuery(id+"F1.opExtrude","CAP_EDGE",EDGE,{"disambiguationData":[OSD([sQuery(id+"F0.wireOp",EDGE,"E154")])],"isStart":true});
            fillet(context, id + "F4", {"entities" : qUnion([Q0, Q1, Q2, Q3]), "radius" : 1 * mm, "tangentPropagation" : true, "allowEdgeOverflow" : false});
        }
        {
            var Q0;
            Q0=makeQuery(id+"F1.opExtrude","SWEPT_EDGE",EDGE,{"disambiguationData":[OSD([sQuery(id+"F0.wireOp",EDGE,"E123"),sQuery(id+"F0.wireOp",EDGE,"E155")])]});
            var Q1;
            Q1=makeQuery(id+"F1.opExtrude","SWEPT_EDGE",EDGE,{"disambiguationData":[OSD([sQuery(id+"F0.wireOp",EDGE,"E123"),sQuery(id+"F0.wireOp",EDGE,"E157")])]});
            var Q2;
            Q2=makeQuery(id+"F1.opExtrude","SWEPT_EDGE",EDGE,{"disambiguationData":[OSD([sQuery(id+"F0.wireOp",EDGE,"E156"),sQuery(id+"F0.wireOp",EDGE,"E157")])]});
            var Q3;
            Q3=makeQuery(id+"F1.opExtrude","SWEPT_EDGE",EDGE,{"disambiguationData":[OSD([sQuery(id+"F0.wireOp",EDGE,"E155"),sQuery(id+"F0.wireOp",EDGE,"E156")])]});
            fillet(context, id + "F5", {"entities" : qUnion([Q0, Q1, Q2, Q3]), "radius" : 4 * mm, "tangentPropagation" : true, "allowEdgeOverflow" : false});
        }
        {
            var Q0;
            Q0=makeQuery(id+"F1.opExtrude","CAP_EDGE",EDGE,{"disambiguationData":[OSD([sQuery(id+"F0.wireOp",EDGE,"E155")])],"isStart":false});
            var Q1;
            Q1=makeQuery(id+"F1.opExtrude","CAP_EDGE",EDGE,{"disambiguationData":[OSD([sQuery(id+"F0.wireOp",EDGE,"E157")])],"isStart":true});
            fillet(context, id + "F6", {"entities" : qUnion([Q0, Q1]), "radius" : 1.5 * mm, "tangentPropagation" : true, "allowEdgeOverflow" : false});
        }
    });
